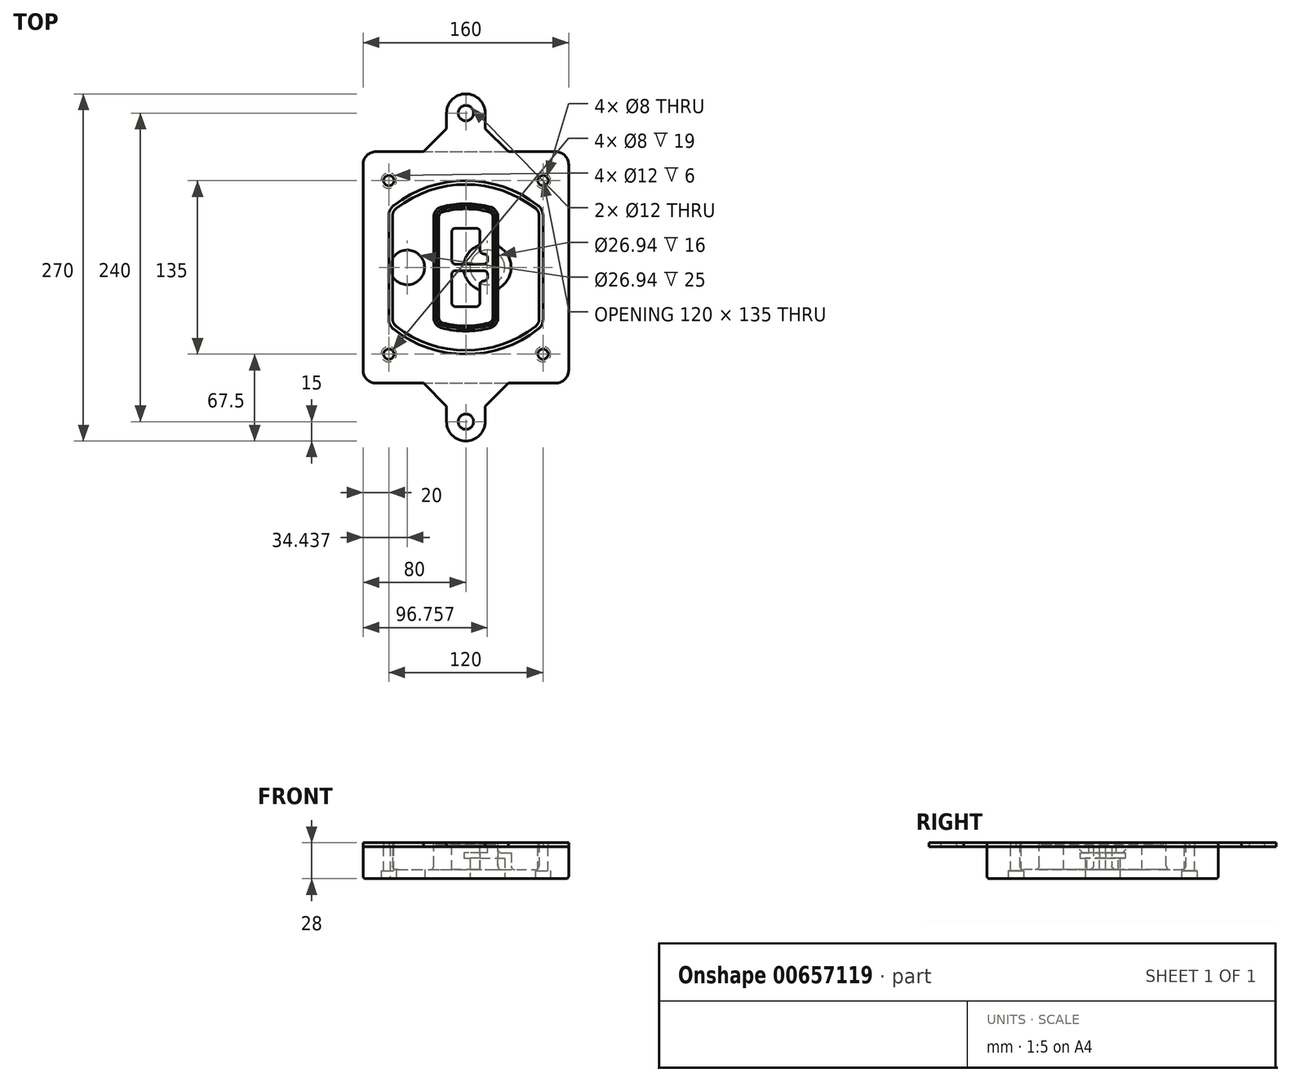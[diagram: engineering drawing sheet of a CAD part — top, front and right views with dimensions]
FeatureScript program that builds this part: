
annotation { "Feature Type Name" : "Feature", "Feature Type Description" : "" }
export const myFeature = defineFeature(function(context is Context, id is Id, definition is map)
    precondition{}
    {
        {
            var Q0;
            Q0=qCreatedBy(makeId("Top.planeOp"),FACE);
            var sketch = newSketch(context, id + "F0", { "sketchPlane" : qUnion([Q0])});
            skPoint(sketch, "E0.rect.middle", {"position": v(0, 0) * mm});
            skLineSegment(sketch, "E1.bottom", {"start": v(-70, -90) * mm, "end": v(70, -90) * mm});
            skLineSegment(sketch, "E1.top", {"start": v(-70, 90) * mm, "end": v(70, 90) * mm});
            skLineSegment(sketch, "E1.left", {"start": v(-80, -80) * mm, "end": v(-80, 80) * mm});
            skLineSegment(sketch, "E1.right", {"start": v(80, -80) * mm, "end": v(80, 80) * mm});
            skLineSegment(sketch, "E2", {"start": v(-80, 90) * mm, "end": v(80, -90) * mm, "construction": true});
            skLineSegment(sketch, "E3", {"start": v(80, 90) * mm, "end": v(-80, -90) * mm, "construction": true});
            skCircle(sketch, "E4", {"center": v(-60, 67.5) * mm, "radius": 4 * mm});
            skCircle(sketch, "E5", {"center": v(60, 67.5) * mm, "radius": 4 * mm});
            skCircle(sketch, "E6", {"center": v(60, -67.5) * mm, "radius": 4 * mm});
            skCircle(sketch, "E7", {"center": v(-60, -67.5) * mm, "radius": 4 * mm});
            skLineSegment(sketch, "E8", {"start": v(-60, 67.5) * mm, "end": v(60, 67.5) * mm, "construction": true});
            skLineSegment(sketch, "E9", {"start": v(60, 67.5) * mm, "end": v(60, -67.5) * mm, "construction": true});
            skLineSegment(sketch, "E10", {"start": v(60, -67.5) * mm, "end": v(-60, -67.5) * mm, "construction": true});
            skLineSegment(sketch, "E11", {"start": v(-60, -67.5) * mm, "end": v(-60, 67.5) * mm, "construction": true});
            skLineSegment(sketch, "E12", {"start": v(-60, 40.3) * mm, "end": v(-60, -40.3) * mm});
            skLineSegment(sketch, "E13", {"start": v(60, 40.3) * mm, "end": v(60, -40.3) * mm});
            skArc(sketch, "E14", {"start": v(56.15, 48.18) * mm, "mid": v(0, 67.5) * mm, "end": v(-56.15, 48.18) * mm});
            skArc(sketch, "E15", {"start": v(-56.15, -48.18) * mm, "mid": v(0, -67.5) * mm, "end": v(56.15, -48.18) * mm});
            skLineSegment(sketch, "E16", {"start": v(-60, 0) * mm, "end": v(60, 0) * mm, "construction": true});
            skPoint(sketch, "E17.visualSharp", {"position": v(-60, -45) * mm});
            skArc(sketch, "E17.filletArc", {"start": v(-60, -40.3) * mm, "mid": v(-58.99, -44.68) * mm, "end": v(-56.15, -48.18) * mm});
            skPoint(sketch, "E18.visualSharp", {"position": v(-60, 45) * mm});
            skArc(sketch, "E18.filletArc", {"start": v(-56.15, 48.18) * mm, "mid": v(-58.99, 44.68) * mm, "end": v(-60, 40.3) * mm});
            skPoint(sketch, "E19.visualSharp", {"position": v(60, 45) * mm});
            skArc(sketch, "E19.filletArc", {"start": v(60, 40.3) * mm, "mid": v(58.99, 44.68) * mm, "end": v(56.15, 48.18) * mm});
            skPoint(sketch, "E20.visualSharp", {"position": v(60, -45) * mm});
            skArc(sketch, "E20.filletArc", {"start": v(56.15, -48.18) * mm, "mid": v(58.99, -44.68) * mm, "end": v(60, -40.3) * mm});
            skPoint(sketch, "E21.visualSharp", {"position": v(-80, 90) * mm});
            skArc(sketch, "E21.filletArc", {"start": v(-70, 90) * mm, "mid": v(-77.07, 87.07) * mm, "end": v(-80, 80) * mm});
            skPoint(sketch, "E22.visualSharp", {"position": v(80, 90) * mm});
            skArc(sketch, "E22.filletArc", {"start": v(80, 80) * mm, "mid": v(77.07, 87.07) * mm, "end": v(70, 90) * mm});
            skPoint(sketch, "E23.visualSharp", {"position": v(80, -90) * mm});
            skArc(sketch, "E23.filletArc", {"start": v(70, -90) * mm, "mid": v(77.07, -87.07) * mm, "end": v(80, -80) * mm});
            skPoint(sketch, "E24.visualSharp", {"position": v(-80, -90) * mm});
            skArc(sketch, "E24.filletArc", {"start": v(-80, -80) * mm, "mid": v(-77.07, -87.07) * mm, "end": v(-70, -90) * mm});
            skArc(sketch, "E25.0", {"start": v(57, 40.3) * mm, "mid": v(56.3, 43.36) * mm, "end": v(54.3, 45.81) * mm});
            skLineSegment(sketch, "E25.1", {"start": v(57, 40.3) * mm, "end": v(57, -40.3) * mm});
            skArc(sketch, "E25.2", {"start": v(54.3, -45.81) * mm, "mid": v(56.3, -43.36) * mm, "end": v(57, -40.3) * mm});
            skArc(sketch, "E25.3", {"start": v(-54.3, -45.81) * mm, "mid": v(0, -64.5) * mm, "end": v(54.3, -45.81) * mm});
            skArc(sketch, "E25.4", {"start": v(-57, -40.3) * mm, "mid": v(-56.3, -43.36) * mm, "end": v(-54.3, -45.81) * mm});
            skArc(sketch, "E25.5", {"start": v(54.3, 45.81) * mm, "mid": v(0, 64.5) * mm, "end": v(-54.3, 45.81) * mm});
            skLineSegment(sketch, "E25.6", {"start": v(-57, 40.3) * mm, "end": v(-57, -40.3) * mm});
            skArc(sketch, "E25.7", {"start": v(-54.3, 45.81) * mm, "mid": v(-56.3, 43.36) * mm, "end": v(-57, 40.3) * mm});
            skArc(sketch, "E26.0", {"start": v(-58.62, 51.33) * mm, "mid": v(-62.58, 46.43) * mm, "end": v(-64, 40.3) * mm});
            skArc(sketch, "E26.1", {"start": v(58.62, 51.33) * mm, "mid": v(0, 71.5) * mm, "end": v(-58.62, 51.33) * mm});
            skArc(sketch, "E26.2", {"start": v(64, 40.3) * mm, "mid": v(62.58, 46.43) * mm, "end": v(58.62, 51.33) * mm});
            skLineSegment(sketch, "E26.3", {"start": v(64, 40.3) * mm, "end": v(64, -40.3) * mm});
            skArc(sketch, "E26.4", {"start": v(58.62, -51.33) * mm, "mid": v(62.58, -46.43) * mm, "end": v(64, -40.3) * mm});
            skLineSegment(sketch, "E26.5", {"start": v(-64, 40.3) * mm, "end": v(-64, -40.3) * mm});
            skArc(sketch, "E26.6", {"start": v(-58.62, -51.33) * mm, "mid": v(0, -71.5) * mm, "end": v(58.62, -51.33) * mm});
            skArc(sketch, "E26.7", {"start": v(-64, -40.3) * mm, "mid": v(-62.58, -46.43) * mm, "end": v(-58.62, -51.33) * mm});
            skSolve(sketch);
        }
        {
            var Q0;
            Q0=makeQuery(id+"F0.imprint","IMPRINT",FACE,{"disambiguationData":[TD([[makeQuery(id+"F0.imprint","IMPRINT",EDGE,{"derivedFrom":sQuery(id+"F0.wireOp",EDGE,"E1.bottom")}),1.0]])]});
            var Q1;
            Q1=makeQuery(id+"F0.imprint","IMPRINT",FACE,{"disambiguationData":[TD([[makeQuery(id+"F0.imprint","IMPRINT",EDGE,{"derivedFrom":sQuery(id+"F0.wireOp",EDGE,"E12")}),1.0]])]});
            var Q2;
            Q2=makeQuery(id+"F0.imprint","IMPRINT",FACE,{"disambiguationData":[TD([[makeQuery(id+"F0.imprint","IMPRINT",EDGE,{"derivedFrom":sQuery(id+"F0.wireOp",EDGE,"E25.0")}),1.0]])]});
            var Q3;
            Q3=makeQuery(id+"F0.imprint","IMPRINT",FACE,{"disambiguationData":[TD([[makeQuery(id+"F0.imprint","IMPRINT",EDGE,{"derivedFrom":sQuery(id+"F0.wireOp",EDGE,"E12")}),-1.0]])]});
            extrude(context, id + "F1", {"entities" : qUnion([Q0, Q1, Q2, Q3]), "oppositeDirection" : true, "depth" : 25 * mm});
        }
        {
            var Q0;
            Q0=makeQuery(id+"F0.imprint","IMPRINT",FACE,{"disambiguationData":[TD([[makeQuery(id+"F0.imprint","IMPRINT",EDGE,{"derivedFrom":sQuery(id+"F0.wireOp",EDGE,"E12")}),1.0]])]});
            extrude(context, id + "F2", {"entities" : qUnion([Q0]), "operationType" : NewBodyOperationType.ADD, "depth" : 3 * mm, "offsetDistance" : 25 * mm});
        }
        {
            var Q0;
            Q0=makeQuery(id+"F0.imprint","IMPRINT",FACE,{"disambiguationData":[TD([[makeQuery(id+"F0.imprint","IMPRINT",EDGE,{"derivedFrom":sQuery(id+"F0.wireOp",EDGE,"E25.0")}),1.0]])]});
            extrude(context, id + "F3", {"entities" : qUnion([Q0]), "operationType" : NewBodyOperationType.REMOVE, "oppositeDirection" : true, "depth" : 18 * mm});
        }
        {
            var Q0;
            Q0=makeQuery(id+"F2.opExtrude","CAP_FACE",FACE,{"disambiguationData":[OSD([sQuery(id+"F0.wireOp",EDGE,"E12"),sQuery(id+"F0.wireOp",EDGE,"E13"),sQuery(id+"F0.wireOp",EDGE,"E14"),sQuery(id+"F0.wireOp",EDGE,"E15"),sQuery(id+"F0.wireOp",EDGE,"E17.filletArc"),sQuery(id+"F0.wireOp",EDGE,"E18.filletArc"),sQuery(id+"F0.wireOp",EDGE,"E19.filletArc"),sQuery(id+"F0.wireOp",EDGE,"E20.filletArc"),sQuery(id+"F0.wireOp",EDGE,"E25.0"),sQuery(id+"F0.wireOp",EDGE,"E25.1"),sQuery(id+"F0.wireOp",EDGE,"E25.2"),sQuery(id+"F0.wireOp",EDGE,"E25.3"),sQuery(id+"F0.wireOp",EDGE,"E25.4"),sQuery(id+"F0.wireOp",EDGE,"E25.5"),sQuery(id+"F0.wireOp",EDGE,"E25.6"),sQuery(id+"F0.wireOp",EDGE,"E25.7")])],"isStart":false});
            var sketch = newSketch(context, id + "F4", { "sketchPlane" : qUnion([Q0])});
            skArc(sketch, "E27.0", {"start": v(-19.08, -46.97) * mm, "mid": v(0, -49.5) * mm, "end": v(19.08, -46.97) * mm});
            skArc(sketch, "E28.0", {"start": v(19.08, 46.97) * mm, "mid": v(0, 49.5) * mm, "end": v(-19.08, 46.97) * mm});
            skLineSegment(sketch, "E29", {"start": v(-25, 39.25) * mm, "end": v(-25, -39.25) * mm});
            skLineSegment(sketch, "E30", {"start": v(25, 39.25) * mm, "end": v(25, -39.25) * mm});
            skLineSegment(sketch, "E31", {"start": v(-25, 45.1) * mm, "end": v(25, 45.1) * mm, "construction": true});
            skLineSegment(sketch, "E32", {"start": v(-25, -45.1) * mm, "end": v(25, -45.1) * mm, "construction": true});
            skPoint(sketch, "E33.visualSharp", {"position": v(-25, 45.1) * mm});
            skArc(sketch, "E33.filletArc", {"start": v(-19.08, 46.97) * mm, "mid": v(-23.35, 44.11) * mm, "end": v(-25, 39.25) * mm});
            skPoint(sketch, "E34.visualSharp", {"position": v(25, 45.1) * mm});
            skArc(sketch, "E34.filletArc", {"start": v(25, 39.25) * mm, "mid": v(23.35, 44.11) * mm, "end": v(19.08, 46.97) * mm});
            skPoint(sketch, "E35.visualSharp", {"position": v(25, -45.1) * mm});
            skArc(sketch, "E35.filletArc", {"start": v(19.08, -46.97) * mm, "mid": v(23.35, -44.11) * mm, "end": v(25, -39.25) * mm});
            skPoint(sketch, "E36.visualSharp", {"position": v(-25, -45.1) * mm});
            skArc(sketch, "E36.filletArc", {"start": v(-25, -39.25) * mm, "mid": v(-23.35, -44.11) * mm, "end": v(-19.08, -46.97) * mm});
            skArc(sketch, "E37.0", {"start": v(54.3, 45.81) * mm, "mid": v(0, 64.5) * mm, "end": v(-54.3, 45.81) * mm});
            skArc(sketch, "E37.1", {"start": v(-54.3, 45.81) * mm, "mid": v(-56.3, 43.36) * mm, "end": v(-57, 40.3) * mm});
            skLineSegment(sketch, "E37.2", {"start": v(-57, 40.3) * mm, "end": v(-57, -40.3) * mm});
            skArc(sketch, "E37.3", {"start": v(-57, -40.3) * mm, "mid": v(-56.3, -43.36) * mm, "end": v(-54.3, -45.81) * mm});
            skArc(sketch, "E37.4", {"start": v(-54.3, -45.81) * mm, "mid": v(0, -64.5) * mm, "end": v(54.3, -45.81) * mm});
            skArc(sketch, "E37.5", {"start": v(54.3, -45.81) * mm, "mid": v(56.3, -43.36) * mm, "end": v(57, -40.3) * mm});
            skLineSegment(sketch, "E37.6", {"start": v(57, 40.3) * mm, "end": v(57, -40.3) * mm});
            skArc(sketch, "E37.7", {"start": v(57, 40.3) * mm, "mid": v(56.3, 43.36) * mm, "end": v(54.3, 45.81) * mm});
            skLineSegment(sketch, "E38.0", {"start": v(23, 39.25) * mm, "end": v(23, -39.25) * mm});
            skArc(sketch, "E38.1", {"start": v(18.56, -45.04) * mm, "mid": v(21.76, -42.9) * mm, "end": v(23, -39.25) * mm});
            skArc(sketch, "E38.2", {"start": v(-18.56, -45.04) * mm, "mid": v(0, -47.5) * mm, "end": v(18.56, -45.04) * mm});
            skArc(sketch, "E38.3", {"start": v(-23, -39.25) * mm, "mid": v(-21.76, -42.9) * mm, "end": v(-18.56, -45.04) * mm});
            skLineSegment(sketch, "E38.4", {"start": v(-23, 39.25) * mm, "end": v(-23, -39.25) * mm});
            skArc(sketch, "E38.5", {"start": v(23, 39.25) * mm, "mid": v(21.76, 42.9) * mm, "end": v(18.56, 45.04) * mm});
            skArc(sketch, "E38.6", {"start": v(-18.56, 45.04) * mm, "mid": v(-21.76, 42.9) * mm, "end": v(-23, 39.25) * mm});
            skArc(sketch, "E38.7", {"start": v(18.56, 45.04) * mm, "mid": v(0, 47.5) * mm, "end": v(-18.56, 45.04) * mm});
            skArc(sketch, "E39.0", {"start": v(21, 39.25) * mm, "mid": v(20.18, 41.68) * mm, "end": v(18.04, 43.1) * mm});
            skLineSegment(sketch, "E39.1", {"start": v(21, 39.25) * mm, "end": v(21, -39.25) * mm});
            skArc(sketch, "E39.2", {"start": v(18.04, -43.1) * mm, "mid": v(20.18, -41.68) * mm, "end": v(21, -39.25) * mm});
            skArc(sketch, "E39.3", {"start": v(-18.04, -43.1) * mm, "mid": v(0, -45.5) * mm, "end": v(18.04, -43.1) * mm});
            skArc(sketch, "E39.4", {"start": v(-21, -39.25) * mm, "mid": v(-20.18, -41.68) * mm, "end": v(-18.04, -43.1) * mm});
            skArc(sketch, "E39.5", {"start": v(18.04, 43.1) * mm, "mid": v(0, 45.5) * mm, "end": v(-18.04, 43.1) * mm});
            skLineSegment(sketch, "E39.6", {"start": v(-21, 39.25) * mm, "end": v(-21, -39.25) * mm});
            skArc(sketch, "E39.7", {"start": v(-18.04, 43.1) * mm, "mid": v(-20.18, 41.68) * mm, "end": v(-21, 39.25) * mm});
            skLineSegment(sketch, "E40", {"start": v(-25, 0) * mm, "end": v(25, 0) * mm, "construction": true});
            skLineSegment(sketch, "E41", {"start": v(-11, 5.5) * mm, "end": v(-11, 27.5) * mm});
            skLineSegment(sketch, "E42", {"start": v(-8, 30.5) * mm, "end": v(8, 30.5) * mm});
            skLineSegment(sketch, "E43", {"start": v(11, 27.5) * mm, "end": v(11, 13.5) * mm});
            skLineSegment(sketch, "E44", {"start": v(14, 10.5) * mm, "end": v(14, 10.5) * mm});
            skLineSegment(sketch, "E45", {"start": v(17, 7.5) * mm, "end": v(17, 5.5) * mm});
            skLineSegment(sketch, "E46", {"start": v(14, 2.5) * mm, "end": v(-8, 2.5) * mm});
            skPoint(sketch, "E47.visualSharp", {"position": v(-11, 30.5) * mm});
            skArc(sketch, "E47.filletArc", {"start": v(-8, 30.5) * mm, "mid": v(-10.12, 29.62) * mm, "end": v(-11, 27.5) * mm});
            skPoint(sketch, "E48.visualSharp", {"position": v(11, 30.5) * mm});
            skArc(sketch, "E48.filletArc", {"start": v(11, 27.5) * mm, "mid": v(10.12, 29.62) * mm, "end": v(8, 30.5) * mm});
            skPoint(sketch, "E49.visualSharp", {"position": v(11, 10.5) * mm});
            skArc(sketch, "E49.filletArc", {"start": v(11, 13.5) * mm, "mid": v(11.88, 11.38) * mm, "end": v(14, 10.5) * mm});
            skPoint(sketch, "E50.visualSharp", {"position": v(17, 10.5) * mm});
            skArc(sketch, "E50.filletArc", {"start": v(17, 7.5) * mm, "mid": v(16.12, 9.62) * mm, "end": v(14, 10.5) * mm});
            skPoint(sketch, "E51.visualSharp", {"position": v(17, 2.5) * mm});
            skArc(sketch, "E51.filletArc", {"start": v(14, 2.5) * mm, "mid": v(16.12, 3.38) * mm, "end": v(17, 5.5) * mm});
            skPoint(sketch, "E52.visualSharp", {"position": v(-11, 2.5) * mm});
            skArc(sketch, "E52.filletArc", {"start": v(-11, 5.5) * mm, "mid": v(-10.12, 3.38) * mm, "end": v(-8, 2.5) * mm});
            skLineSegment(sketch, "E53.0.MirrorCS", {"start": v(14, -2.5) * mm, "end": v(-8, -2.5) * mm});
            skArc(sketch, "E54.0.MirrorCS", {"start": v(-11, -5.5) * mm, "mid": v(-10.12, -3.38) * mm, "end": v(-8, -2.5) * mm});
            skLineSegment(sketch, "E55.0.MirrorCS", {"start": v(-11, -5.5) * mm, "end": v(-11, -27.5) * mm});
            skArc(sketch, "E56.0.MirrorCS", {"start": v(-8, -30.5) * mm, "mid": v(-10.12, -29.62) * mm, "end": v(-11, -27.5) * mm});
            skLineSegment(sketch, "E57.0.MirrorCS", {"start": v(-8, -30.5) * mm, "end": v(8, -30.5) * mm});
            skArc(sketch, "E58.0.MirrorCS", {"start": v(11, -27.5) * mm, "mid": v(10.12, -29.62) * mm, "end": v(8, -30.5) * mm});
            skLineSegment(sketch, "E59.0.MirrorCS", {"start": v(11, -27.5) * mm, "end": v(11, -13.5) * mm});
            skArc(sketch, "E60.0.MirrorCS", {"start": v(11, -13.5) * mm, "mid": v(11.88, -11.38) * mm, "end": v(14, -10.5) * mm});
            skArc(sketch, "E61.0.MirrorCS", {"start": v(17, -7.5) * mm, "mid": v(16.12, -9.62) * mm, "end": v(14, -10.5) * mm});
            skLineSegment(sketch, "E62.0.MirrorCS", {"start": v(17, -7.5) * mm, "end": v(17, -5.5) * mm});
            skArc(sketch, "E63.0.MirrorCS", {"start": v(14, -2.5) * mm, "mid": v(16.12, -3.38) * mm, "end": v(17, -5.5) * mm});
            skSolve(sketch);
        }
        {
            var Q0;
            Q0=makeQuery(id+"F4.imprint","IMPRINT",FACE,{"disambiguationData":[TD([[makeQuery(id+"F4.imprint","IMPRINT",EDGE,{"derivedFrom":sQuery(id+"F4.wireOp",EDGE,"E27.0")}),1.0]])]});
            var Q1;
            Q1=makeQuery(id+"F4.imprint","IMPRINT",FACE,{"disambiguationData":[TD([[makeQuery(id+"F4.imprint","IMPRINT",EDGE,{"derivedFrom":sQuery(id+"F4.wireOp",EDGE,"E38.0")}),-1.0]])]});
            var Q2;
            Q2=makeQuery(id+"F4.imprint","IMPRINT",FACE,{"disambiguationData":[TD([[makeQuery(id+"F4.imprint","IMPRINT",EDGE,{"derivedFrom":sQuery(id+"F4.wireOp",EDGE,"E39.0")}),1.0]])]});
            extrude(context, id + "F5", {"entities" : qUnion([Q0, Q1, Q2]), "operationType" : NewBodyOperationType.ADD, "endBound" : BoundingType.UP_TO_NEXT, "oppositeDirection" : true, "depth" : 25 * mm});
        }
        {
            var Q0;
            Q0=makeQuery(id+"F4.imprint","IMPRINT",FACE,{"disambiguationData":[TD([[makeQuery(id+"F4.imprint","IMPRINT",EDGE,{"derivedFrom":sQuery(id+"F4.wireOp",EDGE,"E38.0")}),-1.0]])]});
            extrude(context, id + "F6", {"entities" : qUnion([Q0]), "operationType" : NewBodyOperationType.REMOVE, "oppositeDirection" : true, "depth" : 2 * mm});
        }
        {
            var Q0;
            Q0=makeQuery(id+"F1.opExtrude","CAP_FACE",FACE,{"disambiguationData":[OSD([sQuery(id+"F0.wireOp",EDGE,"E1.bottom"),sQuery(id+"F0.wireOp",EDGE,"E1.top"),sQuery(id+"F0.wireOp",EDGE,"E1.left"),sQuery(id+"F0.wireOp",EDGE,"E1.right"),sQuery(id+"F0.wireOp",EDGE,"E4"),sQuery(id+"F0.wireOp",EDGE,"E5"),sQuery(id+"F0.wireOp",EDGE,"E6"),sQuery(id+"F0.wireOp",EDGE,"E7"),sQuery(id+"F0.wireOp",EDGE,"E21.filletArc"),sQuery(id+"F0.wireOp",EDGE,"E22.filletArc"),sQuery(id+"F0.wireOp",EDGE,"E23.filletArc"),sQuery(id+"F0.wireOp",EDGE,"E24.filletArc")])],"isStart":false});
            var sketch = newSketch(context, id + "F7", { "sketchPlane" : qUnion([Q0])});
            skCircle(sketch, "E64", {"center": v(16.76, 0) * mm, "radius": 13.47 * mm});
            skCircle(sketch, "E65", {"center": v(-45.56, 0) * mm, "radius": 13.47 * mm});
            skLineSegment(sketch, "E66", {"start": v(80, 0) * mm, "end": v(-80, 0) * mm});
            skCircle(sketch, "E67", {"center": v(16.76, 0) * mm, "radius": 18.47 * mm});
            skCircle(sketch, "E68", {"center": v(60, -67.5) * mm, "radius": 6 * mm});
            skCircle(sketch, "E69", {"center": v(-60, -67.5) * mm, "radius": 6 * mm});
            skCircle(sketch, "E70", {"center": v(-60, 67.5) * mm, "radius": 6 * mm});
            skCircle(sketch, "E71", {"center": v(60, 67.5) * mm, "radius": 6 * mm});
            skSolve(sketch);
        }
        {
            var Q0;
            {var subQ1=sQuery(id+"F7.wireOp",EDGE,"E66");var subQ4=sQuery(id+"F7.wireOp",EDGE,"E64");var subQ6=makeQuery(id+"F7.imprint","INTERSECT",VERTEX,{"disambiguationData":[OD(0.0)],"derivedFrom":[subQ4,subQ1]});Q0=makeQuery(id+"F7.imprint","IMPRINT",FACE,{"disambiguationData":[TD([[makeQuery(id+"F7.imprint","IMPRINT",EDGE,{"disambiguationData":[TD([[subQ6,-1.0]])],"derivedFrom":subQ4}),-1.0]])]});}
            var Q1;
            {var subQ0=sQuery(id+"F7.wireOp",EDGE,"E66");var subQ1=sQuery(id+"F7.wireOp",EDGE,"E64");var subQ3=makeQuery(id+"F7.imprint","INTERSECT",VERTEX,{"disambiguationData":[OD(0.0)],"derivedFrom":[subQ1,subQ0]});Q1=makeQuery(id+"F7.imprint","IMPRINT",FACE,{"disambiguationData":[TD([[makeQuery(id+"F7.imprint","IMPRINT",EDGE,{"disambiguationData":[TD([[subQ3,-1.0]])],"derivedFrom":subQ1}),1.0]])]});}
            var Q2;
            {var subQ0=sQuery(id+"F7.wireOp",EDGE,"E66");var subQ1=sQuery(id+"F7.wireOp",EDGE,"E64");var subQ3=makeQuery(id+"F7.imprint","INTERSECT",VERTEX,{"disambiguationData":[OD(0.0)],"derivedFrom":[subQ1,subQ0]});Q2=makeQuery(id+"F7.imprint","IMPRINT",FACE,{"disambiguationData":[TD([[makeQuery(id+"F7.imprint","IMPRINT",EDGE,{"disambiguationData":[TD([[subQ3,1.0]])],"derivedFrom":subQ1}),1.0]])]});}
            var Q3;
            {var subQ1=sQuery(id+"F7.wireOp",EDGE,"E66");var subQ4=sQuery(id+"F7.wireOp",EDGE,"E64");var subQ6=makeQuery(id+"F7.imprint","INTERSECT",VERTEX,{"disambiguationData":[OD(0.0)],"derivedFrom":[subQ4,subQ1]});Q3=makeQuery(id+"F7.imprint","IMPRINT",FACE,{"disambiguationData":[TD([[makeQuery(id+"F7.imprint","IMPRINT",EDGE,{"disambiguationData":[TD([[subQ6,1.0]])],"derivedFrom":subQ4}),-1.0]])]});}
            extrude(context, id + "F8", {"entities" : qUnion([Q0, Q1, Q2, Q3]), "operationType" : NewBodyOperationType.ADD, "oppositeDirection" : true, "depth" : 20 * mm});
        }
        {
            var Q0;
            {var subQ0=sQuery(id+"F7.wireOp",EDGE,"E66");var subQ1=sQuery(id+"F7.wireOp",EDGE,"E64");var subQ3=makeQuery(id+"F7.imprint","INTERSECT",VERTEX,{"disambiguationData":[OD(0.0)],"derivedFrom":[subQ1,subQ0]});Q0=makeQuery(id+"F7.imprint","IMPRINT",FACE,{"disambiguationData":[TD([[makeQuery(id+"F7.imprint","IMPRINT",EDGE,{"disambiguationData":[TD([[subQ3,-1.0]])],"derivedFrom":subQ1}),1.0]])]});}
            var Q1;
            {var subQ0=sQuery(id+"F7.wireOp",EDGE,"E66");var subQ1=sQuery(id+"F7.wireOp",EDGE,"E64");var subQ3=makeQuery(id+"F7.imprint","INTERSECT",VERTEX,{"disambiguationData":[OD(0.0)],"derivedFrom":[subQ1,subQ0]});Q1=makeQuery(id+"F7.imprint","IMPRINT",FACE,{"disambiguationData":[TD([[makeQuery(id+"F7.imprint","IMPRINT",EDGE,{"disambiguationData":[TD([[subQ3,1.0]])],"derivedFrom":subQ1}),1.0]])]});}
            extrude(context, id + "F9", {"entities" : qUnion([Q0, Q1]), "operationType" : NewBodyOperationType.REMOVE, "oppositeDirection" : true, "depth" : 16 * mm});
        }
        {
            var Q0;
            {var subQ0=sQuery(id+"F7.wireOp",EDGE,"E66");var subQ1=sQuery(id+"F7.wireOp",EDGE,"E65");var subQ3=makeQuery(id+"F7.imprint","INTERSECT",VERTEX,{"disambiguationData":[OD(0.0)],"derivedFrom":[subQ1,subQ0]});Q0=makeQuery(id+"F7.imprint","IMPRINT",FACE,{"disambiguationData":[TD([[makeQuery(id+"F7.imprint","IMPRINT",EDGE,{"disambiguationData":[TD([[subQ3,-1.0]])],"derivedFrom":subQ1}),1.0]])]});}
            var Q1;
            {var subQ0=sQuery(id+"F7.wireOp",EDGE,"E66");var subQ1=sQuery(id+"F7.wireOp",EDGE,"E65");var subQ3=makeQuery(id+"F7.imprint","INTERSECT",VERTEX,{"disambiguationData":[OD(0.0)],"derivedFrom":[subQ1,subQ0]});Q1=makeQuery(id+"F7.imprint","IMPRINT",FACE,{"disambiguationData":[TD([[makeQuery(id+"F7.imprint","IMPRINT",EDGE,{"disambiguationData":[TD([[subQ3,1.0]])],"derivedFrom":subQ1}),1.0]])]});}
            extrude(context, id + "F10", {"entities" : qUnion([Q0, Q1]), "operationType" : NewBodyOperationType.REMOVE, "oppositeDirection" : true, "depth" : 25 * mm});
        }
        {
            var Q0;
            Q0=makeQuery(id+"F7.imprint","IMPRINT",FACE,{"disambiguationData":[TD([[makeQuery(id+"F7.imprint","IMPRINT",EDGE,{"derivedFrom":sQuery(id+"F7.wireOp",EDGE,"E68")}),1.0]])]});
            var Q1;
            Q1=makeQuery(id+"F7.imprint","IMPRINT",FACE,{"disambiguationData":[TD([[makeQuery(id+"F7.imprint","IMPRINT",EDGE,{"derivedFrom":makeQuery(id+"F1.opExtrude","CAP_EDGE",EDGE,{"disambiguationData":[OSD([sQuery(id+"F0.wireOp",EDGE,"E5")])],"isStart":false})}),-1.0]])]});
            var Q2;
            Q2=makeQuery(id+"F7.imprint","IMPRINT",FACE,{"disambiguationData":[TD([[makeQuery(id+"F7.imprint","IMPRINT",EDGE,{"derivedFrom":sQuery(id+"F7.wireOp",EDGE,"E69")}),1.0]])]});
            var Q3;
            Q3=makeQuery(id+"F7.imprint","IMPRINT",FACE,{"disambiguationData":[TD([[makeQuery(id+"F7.imprint","IMPRINT",EDGE,{"derivedFrom":makeQuery(id+"F1.opExtrude","CAP_EDGE",EDGE,{"disambiguationData":[OSD([sQuery(id+"F0.wireOp",EDGE,"E4")])],"isStart":false})}),-1.0]])]});
            var Q4;
            Q4=makeQuery(id+"F7.imprint","IMPRINT",FACE,{"disambiguationData":[TD([[makeQuery(id+"F7.imprint","IMPRINT",EDGE,{"derivedFrom":sQuery(id+"F7.wireOp",EDGE,"E70")}),1.0]])]});
            var Q5;
            Q5=makeQuery(id+"F7.imprint","IMPRINT",FACE,{"disambiguationData":[TD([[makeQuery(id+"F7.imprint","IMPRINT",EDGE,{"derivedFrom":makeQuery(id+"F1.opExtrude","CAP_EDGE",EDGE,{"disambiguationData":[OSD([sQuery(id+"F0.wireOp",EDGE,"E7")])],"isStart":false})}),-1.0]])]});
            var Q6;
            Q6=makeQuery(id+"F7.imprint","IMPRINT",FACE,{"disambiguationData":[TD([[makeQuery(id+"F7.imprint","IMPRINT",EDGE,{"derivedFrom":sQuery(id+"F7.wireOp",EDGE,"E71")}),1.0]])]});
            var Q7;
            Q7=makeQuery(id+"F7.imprint","IMPRINT",FACE,{"disambiguationData":[TD([[makeQuery(id+"F7.imprint","IMPRINT",EDGE,{"derivedFrom":makeQuery(id+"F1.opExtrude","CAP_EDGE",EDGE,{"disambiguationData":[OSD([sQuery(id+"F0.wireOp",EDGE,"E6")])],"isStart":false})}),-1.0]])]});
            extrude(context, id + "F11", {"entities" : qUnion([Q0, Q1, Q2, Q3, Q4, Q5, Q6, Q7]), "operationType" : NewBodyOperationType.REMOVE, "oppositeDirection" : true, "depth" : 6 * mm});
        }
        {
            var Q0;
            Q0=makeQuery(id+"F9.boolean.opBoolean","COPY",FACE,{"derivedFrom":makeQuery(id+"F9.opExtrude","CAP_FACE",FACE,{"disambiguationData":[OSD([sQuery(id+"F7.wireOp",EDGE,"E64")])],"isStart":false})});
            var sketch = newSketch(context, id + "F12", { "sketchPlane" : qUnion([Q0])});
            skArc(sketch, "E72.0", {"start": v(11, 17.55) * mm, "mid": v(2.57, 11.82) * mm, "end": v(-1.54, 2.5) * mm});
            skArc(sketch, "E72.1", {"start": v(-1.54, -2.5) * mm, "mid": v(2.57, -11.82) * mm, "end": v(11, -17.55) * mm});
            skLineSegment(sketch, "E73", {"start": v(-1.54, -2.5) * mm, "end": v(14, -2.5) * mm});
            skLineSegment(sketch, "E74.0", {"start": v(14, 2.5) * mm, "end": v(-1.54, 2.5) * mm});
            skArc(sketch, "E74.1", {"start": v(14, 2.5) * mm, "mid": v(16.12, 3.38) * mm, "end": v(17, 5.5) * mm});
            skLineSegment(sketch, "E74.2", {"start": v(17, 7.5) * mm, "end": v(17, 5.5) * mm});
            skArc(sketch, "E74.3", {"start": v(17, 7.5) * mm, "mid": v(16.12, 9.62) * mm, "end": v(14, 10.5) * mm});
            skArc(sketch, "E74.4", {"start": v(11, 13.5) * mm, "mid": v(11.88, 11.38) * mm, "end": v(14, 10.5) * mm});
            skLineSegment(sketch, "E74.5", {"start": v(11, 17.55) * mm, "end": v(11, 13.5) * mm});
            skLineSegment(sketch, "E74.7", {"start": v(14, -2.5) * mm, "end": v(-1.54, -2.5) * mm});
            skArc(sketch, "E74.8", {"start": v(14, -2.5) * mm, "mid": v(16.12, -3.38) * mm, "end": v(17, -5.5) * mm});
            skLineSegment(sketch, "E74.9", {"start": v(17, -7.5) * mm, "end": v(17, -5.5) * mm});
            skArc(sketch, "E74.10", {"start": v(17, -7.5) * mm, "mid": v(16.12, -9.62) * mm, "end": v(14, -10.5) * mm});
            skArc(sketch, "E74.11", {"start": v(11, -13.5) * mm, "mid": v(11.88, -11.38) * mm, "end": v(14, -10.5) * mm});
            skLineSegment(sketch, "E74.12", {"start": v(11, -17.55) * mm, "end": v(11, -13.5) * mm});
            skPoint(sketch, "E75.orphan", {"position": v(11, -27.5) * mm});
            skPoint(sketch, "E76.orphan", {"position": v(-8, -2.5) * mm});
            skPoint(sketch, "E77.orphan", {"position": v(-8, 2.5) * mm});
            skPoint(sketch, "E78.orphan", {"position": v(11, 27.5) * mm});
            skSolve(sketch);
        }
        {
            var Q0;
            {var subQ7=sQuery(id+"F12.wireOp",EDGE,"E72.0");var subQ14=sQuery(id+"F12.wireOp",EDGE,"E72.1");var subQ16=sQuery(id+"F12.wireOp",EDGE,"E74.1");var subQ18=sQuery(id+"F12.wireOp",EDGE,"E74.8");Q0=qUnion([makeQuery(id+"F12.imprint","IMPRINT",FACE,{"disambiguationData":[TD([[makeQuery(id+"F12.imprint","IMPRINT",EDGE,{"derivedFrom":subQ7}),1.0]])]}),makeQuery(id+"F12.imprint","IMPRINT",FACE,{"disambiguationData":[TD([[makeQuery(id+"F12.imprint","IMPRINT",EDGE,{"derivedFrom":subQ14}),1.0]])]}),makeQuery(id+"F12.imprint","IMPRINT",FACE,{"disambiguationData":[TD([[makeQuery(id+"F12.imprint","IMPRINT",EDGE,{"derivedFrom":subQ16}),1.0]])]}),makeQuery(id+"F12.imprint","IMPRINT",FACE,{"disambiguationData":[TD([[makeQuery(id+"F12.imprint","IMPRINT",EDGE,{"derivedFrom":subQ18}),-1.0]])]})]);}
            var Q1;
            Q1=makeQuery(id+"F5.boolean.opBoolean","SPLIT",FACE,{"disambiguationData":[TD([makeQuery(id+"F5.opExtrude","SWEPT_FACE",FACE,{"disambiguationData":[OSD([sQuery(id+"F4.wireOp",EDGE,"E41")])]})])],"derivedFrom":makeQuery(id+"F3.boolean.opBoolean","COPY",FACE,{"derivedFrom":makeQuery(id+"F3.opExtrude","CAP_FACE",FACE,{"disambiguationData":[OSD([sQuery(id+"F0.wireOp",EDGE,"E25.0"),sQuery(id+"F0.wireOp",EDGE,"E25.1"),sQuery(id+"F0.wireOp",EDGE,"E25.2"),sQuery(id+"F0.wireOp",EDGE,"E25.3"),sQuery(id+"F0.wireOp",EDGE,"E25.4"),sQuery(id+"F0.wireOp",EDGE,"E25.5"),sQuery(id+"F0.wireOp",EDGE,"E25.6"),sQuery(id+"F0.wireOp",EDGE,"E25.7")])],"isStart":false})})});
            extrude(context, id + "F13", {"entities" : qUnion([Q0]), "operationType" : NewBodyOperationType.REMOVE, "endBound" : BoundingType.UP_TO_SURFACE, "endBoundEntityFace" : qUnion([Q1]), "depth" : 25 * mm});
        }
        {
            var Q0;
            Q0=makeQuery(id+"F3.boolean.opBoolean","COPY",EDGE,{"derivedFrom":makeQuery(id+"F3.opExtrude","CAP_EDGE",EDGE,{"disambiguationData":[OSD([sQuery(id+"F0.wireOp",EDGE,"E25.6")])],"isStart":false})});
            var Q1;
            Q1=makeQuery(id+"F8.boolean.opBoolean","INTERSECT",EDGE,{"derivedFrom":[makeQuery(id+"F5.opExtrude","SWEPT_FACE",FACE,{"disambiguationData":[OSD([sQuery(id+"F4.wireOp",EDGE,"E30")])]}),makeQuery(id+"F8.opExtrude","CAP_FACE",FACE,{"disambiguationData":[OSD([sQuery(id+"F7.wireOp",EDGE,"E67")])],"isStart":false})]});
            var Q2;
            Q2=makeQuery(id+"F8.boolean.opBoolean","INTERSECT",EDGE,{"disambiguationData":[OD(1.0)],"derivedFrom":[makeQuery(id+"F5.opExtrude","SWEPT_FACE",FACE,{"disambiguationData":[OSD([sQuery(id+"F4.wireOp",EDGE,"E30")])]}),makeQuery(id+"F8.opExtrude","SWEPT_FACE",FACE,{"disambiguationData":[OSD([sQuery(id+"F7.wireOp",EDGE,"E67")])]})]});
            var Q3;
            {var subQ0=sQuery(id+"F4.wireOp",EDGE,"E30");Q3=makeQuery(id+"F8.boolean.opBoolean","SPLIT",EDGE,{"disambiguationData":[TD([makeQuery(id+"F5.opExtrude","SWEPT_FACE",FACE,{"disambiguationData":[OSD([sQuery(id+"F4.wireOp",EDGE,"E35.filletArc")])]})])],"derivedFrom":makeQuery(id+"F5.opExtrude","CAP_EDGE",EDGE,{"disambiguationData":[OSD([subQ0])],"isStart":false})});}
            var Q4;
            {var subQ0=sQuery(id+"F0.wireOp",EDGE,"E25.7");var subQ1=sQuery(id+"F0.wireOp",EDGE,"E25.1");var subQ2=sQuery(id+"F0.wireOp",EDGE,"E25.6");var subQ3=sQuery(id+"F0.wireOp",EDGE,"E25.5");var subQ4=sQuery(id+"F0.wireOp",EDGE,"E25.4");var subQ5=sQuery(id+"F0.wireOp",EDGE,"E25.0");var subQ6=sQuery(id+"F0.wireOp",EDGE,"E25.2");var subQ7=sQuery(id+"F0.wireOp",EDGE,"E25.3");Q4=makeQuery(id+"F8.boolean.opBoolean","INTERSECT",EDGE,{"derivedFrom":[makeQuery(id+"F5.boolean.opBoolean","SPLIT",FACE,{"disambiguationData":[TD([makeQuery(id+"F2.opExtrude","SWEPT_FACE",FACE,{"disambiguationData":[OSD([subQ5])]})])],"derivedFrom":makeQuery(id+"F3.boolean.opBoolean","COPY",FACE,{"derivedFrom":makeQuery(id+"F3.opExtrude","CAP_FACE",FACE,{"disambiguationData":[OSD([subQ5,subQ1,subQ6,subQ7,subQ4,subQ3,subQ2,subQ0])],"isStart":false})})}),makeQuery(id+"F8.opExtrude","SWEPT_FACE",FACE,{"disambiguationData":[OSD([sQuery(id+"F7.wireOp",EDGE,"E67")])]})]});}
            var Q5;
            Q5=makeQuery(id+"F8.boolean.opBoolean","INTERSECT",EDGE,{"disambiguationData":[OD(0.0)],"derivedFrom":[makeQuery(id+"F5.opExtrude","SWEPT_FACE",FACE,{"disambiguationData":[OSD([sQuery(id+"F4.wireOp",EDGE,"E30")])]}),makeQuery(id+"F8.opExtrude","SWEPT_FACE",FACE,{"disambiguationData":[OSD([sQuery(id+"F7.wireOp",EDGE,"E67")])]})]});
            fillet(context, id + "F14", {"entities" : qUnion([Q0, Q1, Q2, Q3, Q4, Q5]), "radius" : 3 * mm, "tangentPropagation" : true, "allowEdgeOverflow" : false});
        }
        {
            var Q0;
            Q0=makeQuery(id+"F1.opExtrude","CAP_EDGE",EDGE,{"disambiguationData":[OSD([sQuery(id+"F0.wireOp",EDGE,"E1.bottom")])],"isStart":false});
            fillet(context, id + "F15", {"entities" : qUnion([Q0]), "radius" : 2 * mm, "tangentPropagation" : true, "allowEdgeOverflow" : false});
        }
        {
            var Q0;
            {var subQ0=sQuery(id+"F0.wireOp",EDGE,"E21.filletArc");var subQ1=sQuery(id+"F0.wireOp",EDGE,"E7");var subQ2=sQuery(id+"F0.wireOp",EDGE,"E6");var subQ3=sQuery(id+"F0.wireOp",EDGE,"E5");var subQ4=sQuery(id+"F0.wireOp",EDGE,"E4");var subQ5=sQuery(id+"F0.wireOp",EDGE,"E22.filletArc");var subQ6=sQuery(id+"F0.wireOp",EDGE,"E1.bottom");var subQ7=sQuery(id+"F0.wireOp",EDGE,"E1.right");var subQ8=sQuery(id+"F0.wireOp",EDGE,"E1.top");var subQ9=sQuery(id+"F0.wireOp",EDGE,"E1.left");var subQ10=sQuery(id+"F0.wireOp",EDGE,"E23.filletArc");var subQ11=sQuery(id+"F0.wireOp",EDGE,"E24.filletArc");Q0=makeQuery(id+"F2.boolean.opBoolean","SPLIT",FACE,{"disambiguationData":[TD([makeQuery(id+"F1.opExtrude","SWEPT_FACE",FACE,{"disambiguationData":[OSD([subQ6])]})])],"derivedFrom":makeQuery(id+"F1.opExtrude","CAP_FACE",FACE,{"disambiguationData":[OSD([subQ6,subQ8,subQ9,subQ7,subQ4,subQ3,subQ2,subQ1,subQ0,subQ5,subQ10,subQ11])],"isStart":true})});}
            var sketch = newSketch(context, id + "F16", { "sketchPlane" : qUnion([Q0])});
            skLineSegment(sketch, "E79", {"start": v(0, 90) * mm, "end": v(0, 120) * mm, "construction": true});
            skLineSegment(sketch, "E80", {"start": v(-33, 90) * mm, "end": v(-15, 108) * mm});
            skLineSegment(sketch, "E81", {"start": v(-15, 108) * mm, "end": v(-15, 120) * mm});
            skLineSegment(sketch, "E82.MirrorCS", {"start": v(15, 108) * mm, "end": v(15, 120) * mm});
            skLineSegment(sketch, "E83.MirrorCS", {"start": v(33, 90) * mm, "end": v(15, 108) * mm});
            skArc(sketch, "E84", {"start": v(15, 120) * mm, "mid": v(0, 135) * mm, "end": v(-15, 120) * mm});
            skCircle(sketch, "E85", {"center": v(0, 120) * mm, "radius": 6 * mm});
            skLineSegment(sketch, "E86.MirrorCS", {"start": v(-33, -90) * mm, "end": v(-15, -108) * mm});
            skLineSegment(sketch, "E87.MirrorCS", {"start": v(-15, -108) * mm, "end": v(-15, -120) * mm});
            skArc(sketch, "E88.MirrorCS", {"start": v(15, -120) * mm, "mid": v(0, -135) * mm, "end": v(-15, -120) * mm});
            skCircle(sketch, "E89.MirrorC", {"center": v(0, -120) * mm, "radius": 6 * mm});
            skLineSegment(sketch, "E90.MirrorCS", {"start": v(0, -90) * mm, "end": v(0, -120) * mm, "construction": true});
            skLineSegment(sketch, "E91.MirrorCS", {"start": v(33, -90) * mm, "end": v(15, -108) * mm});
            skLineSegment(sketch, "E92.MirrorCS", {"start": v(15, -108) * mm, "end": v(15, -120) * mm});
            skSolve(sketch);
        }
        {
            var Q0;
            Q0=makeQuery(id+"F16.imprint","IMPRINT",FACE,{"disambiguationData":[TD([[makeQuery(id+"F16.imprint","IMPRINT",EDGE,{"derivedFrom":makeQuery(id+"F1.opExtrude","CAP_EDGE",EDGE,{"disambiguationData":[OSD([sQuery(id+"F0.wireOp",EDGE,"E1.left")])],"isStart":true})}),-1.0]])]});
            var Q1;
            {var subQ0=sQuery(id+"F16.wireOp",EDGE,"E86.MirrorCS");Q1=makeQuery(id+"F16.imprint","IMPRINT",FACE,{"disambiguationData":[TD([[makeQuery(id+"F16.imprint","IMPRINT",EDGE,{"derivedFrom":subQ0}),1.0]])]});}
            var Q2;
            {var subQ1=sQuery(id+"F16.wireOp",EDGE,"E80");Q2=makeQuery(id+"F16.imprint","IMPRINT",FACE,{"disambiguationData":[TD([[makeQuery(id+"F16.imprint","IMPRINT",EDGE,{"derivedFrom":subQ1}),-1.0]])]});}
            var Q3;
            Q3 = qConstructionFilter(qBodyType(qCreatedBy(id + "F16" ,EDGE), BodyType.WIRE), ConstructionObject.NO);
            var Q4;
            Q4=makeQuery(id+"F2.opExtrude","CAP_FACE",FACE,{"disambiguationData":[OSD([sQuery(id+"F0.wireOp",EDGE,"E12"),sQuery(id+"F0.wireOp",EDGE,"E13"),sQuery(id+"F0.wireOp",EDGE,"E14"),sQuery(id+"F0.wireOp",EDGE,"E15"),sQuery(id+"F0.wireOp",EDGE,"E17.filletArc"),sQuery(id+"F0.wireOp",EDGE,"E18.filletArc"),sQuery(id+"F0.wireOp",EDGE,"E19.filletArc"),sQuery(id+"F0.wireOp",EDGE,"E20.filletArc"),sQuery(id+"F0.wireOp",EDGE,"E25.0"),sQuery(id+"F0.wireOp",EDGE,"E25.1"),sQuery(id+"F0.wireOp",EDGE,"E25.2"),sQuery(id+"F0.wireOp",EDGE,"E25.3"),sQuery(id+"F0.wireOp",EDGE,"E25.4"),sQuery(id+"F0.wireOp",EDGE,"E25.5"),sQuery(id+"F0.wireOp",EDGE,"E25.6"),sQuery(id+"F0.wireOp",EDGE,"E25.7")])],"isStart":false});
            extrude(context, id + "F17", {"entities" : qUnion([Q0, Q1, Q2]), "surfaceEntities" : qUnion([Q3]), "endBound" : BoundingType.UP_TO_SURFACE, "depth" : 25 * mm, "endBoundEntityFace" : qUnion([Q4]), "offsetDistance" : 25 * mm});
        }
    });
